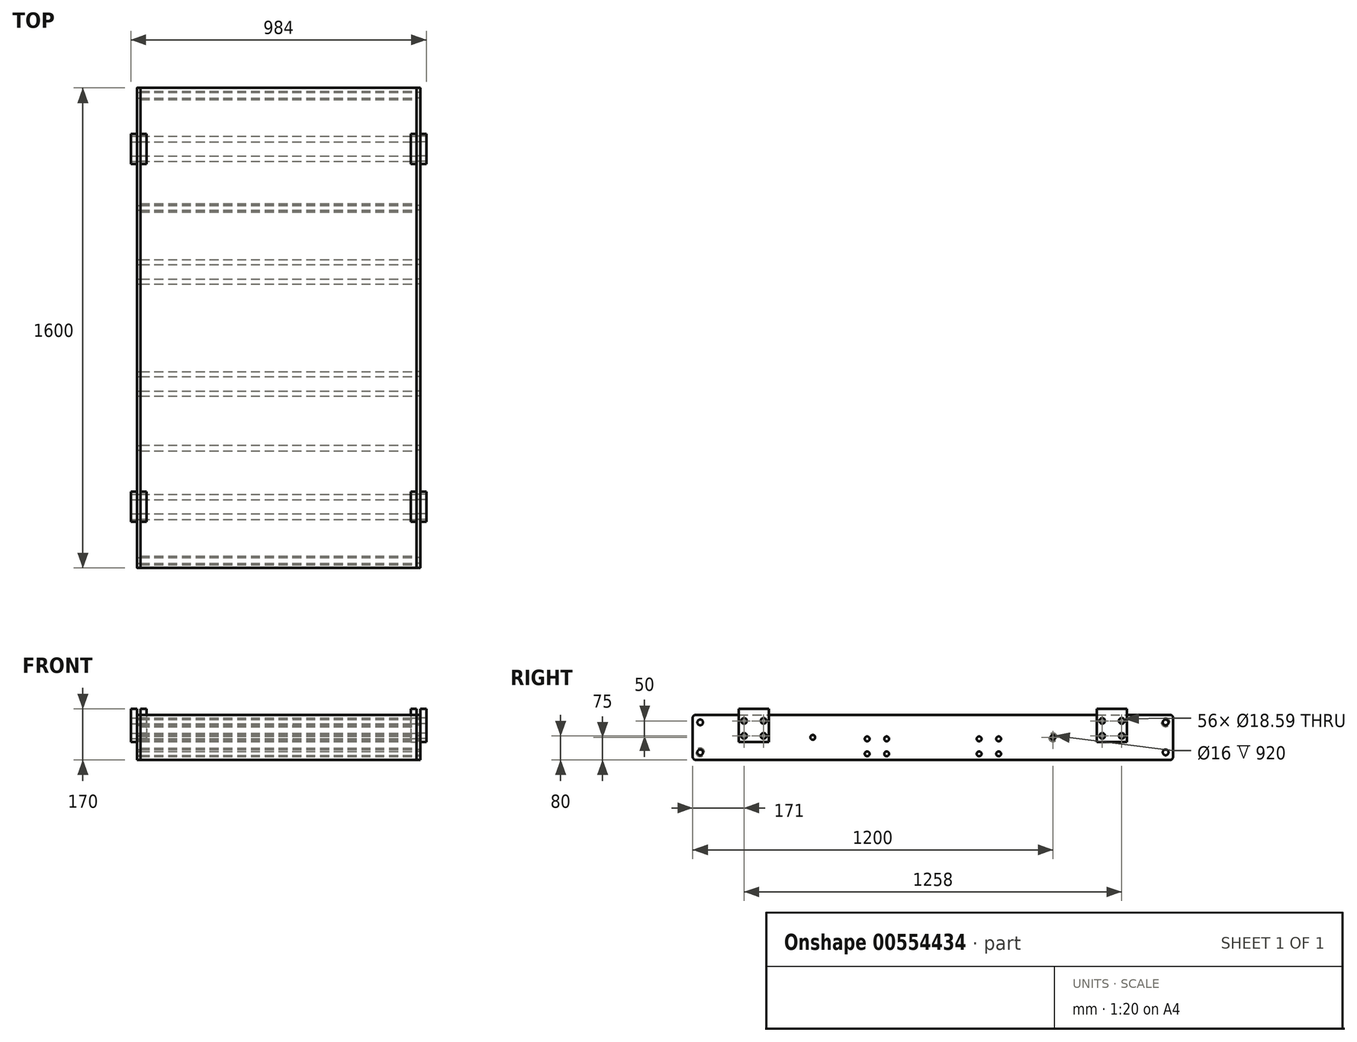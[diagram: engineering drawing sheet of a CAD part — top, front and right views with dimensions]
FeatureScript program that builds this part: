
annotation { "Feature Type Name" : "Feature", "Feature Type Description" : "" }
export const myFeature = defineFeature(function(context is Context, id is Id, definition is map)
    precondition{}
    {
        {
            var Q0;
            Q0=qCreatedBy(makeId("Right.planeOp"),FACE);
            var sketch = newSketch(context, id + "F0", { "sketchPlane" : qUnion([Q0])});
            skLineSegment(sketch, "E0.bottom", {"start": v(-790, 75) * mm, "end": v(790, 75) * mm});
            skLineSegment(sketch, "E0.top", {"start": v(-790, -75) * mm, "end": v(790, -75) * mm});
            skLineSegment(sketch, "E0.left", {"start": v(-800, 65) * mm, "end": v(-800, -65) * mm});
            skLineSegment(sketch, "E0.right", {"start": v(800, 65) * mm, "end": v(800, -65) * mm});
            skPoint(sketch, "E0.middle", {"position": v(0, 0) * mm});
            skLineSegment(sketch, "E1", {"start": v(0, 0) * mm, "end": v(610, 0) * mm, "construction": true});
            skLineSegment(sketch, "E2", {"start": v(0, 0) * mm, "end": v(-610, 0) * mm, "construction": true});
            skLineSegment(sketch, "E3.0", {"start": v(-800, -36.9) * mm, "end": v(800, -36.9) * mm, "construction": true});
            skLineSegment(sketch, "E4.0", {"start": v(-800, 36.9) * mm, "end": v(800, 36.9) * mm, "construction": true});
            skLineSegment(sketch, "E5", {"start": v(610, 36.9) * mm, "end": v(610, -36.9) * mm, "construction": true});
            skLineSegment(sketch, "E6", {"start": v(-610, 36.9) * mm, "end": v(-610, -36.9) * mm, "construction": true});
            skLineSegment(sketch, "E7", {"start": v(610, -36.9) * mm, "end": v(610, -86.9) * mm, "construction": true});
            skPoint(sketch, "E8.visualSharp", {"position": v(-800, 75) * mm});
            skArc(sketch, "E8.filletArc", {"start": v(-790, 75) * mm, "mid": v(-797.07, 72.07) * mm, "end": v(-800, 65) * mm});
            skPoint(sketch, "E9.visualSharp", {"position": v(-800, -75) * mm});
            skArc(sketch, "E9.filletArc", {"start": v(-800, -65) * mm, "mid": v(-797.07, -72.07) * mm, "end": v(-790, -75) * mm});
            skPoint(sketch, "E10.visualSharp", {"position": v(800, 75) * mm});
            skArc(sketch, "E10.filletArc", {"start": v(800, 65) * mm, "mid": v(797.07, 72.07) * mm, "end": v(790, 75) * mm});
            skPoint(sketch, "E11.visualSharp", {"position": v(800, -75) * mm});
            skArc(sketch, "E11.filletArc", {"start": v(790, -75) * mm, "mid": v(797.07, -72.07) * mm, "end": v(800, -65) * mm});
            skCircle(sketch, "E12", {"center": v(-775, 50) * mm, "radius": 9.5 * mm});
            skCircle(sketch, "E13.MirrorC", {"center": v(-775, -50) * mm, "radius": 9.5 * mm});
            skCircle(sketch, "E14.MirrorC", {"center": v(775, -50) * mm, "radius": 9.5 * mm});
            skCircle(sketch, "E15.MirrorC", {"center": v(775, 50) * mm, "radius": 9.5 * mm});
            skCircle(sketch, "E16", {"center": v(-400, 0) * mm, "radius": 8 * mm});
            skCircle(sketch, "E17.MirrorC", {"center": v(400, 0) * mm, "radius": 8 * mm});
            skLineSegment(sketch, "E18", {"start": v(645, -75) * mm, "end": v(645, 137.26) * mm, "construction": true});
            skLineSegment(sketch, "E19", {"start": v(-645, -75) * mm, "end": v(-645, 146.68) * mm, "construction": true});
            skLineSegment(sketch, "E20", {"start": v(-645, 92.82) * mm, "end": v(0, 92.82) * mm, "construction": true});
            skPoint(sketch, "E20.endSnap0", {"position": v(0, 75) * mm});
            skLineSegment(sketch, "E21", {"start": v(0, 92.82) * mm, "end": v(645, 92.82) * mm, "construction": true});
            skLineSegment(sketch, "E22.0", {"start": v(-790, 55) * mm, "end": v(790, 55) * mm, "construction": true});
            skLineSegment(sketch, "E23", {"start": v(-629, 92.82) * mm, "end": v(-629, 0) * mm});
            skPoint(sketch, "E24", {"position": v(-629, 5) * mm});
            skPoint(sketch, "E24.positionSnap0", {"position": v(-629, 46.4) * mm});
            skPoint(sketch, "E25", {"position": v(-629, 55) * mm});
            skLineSegment(sketch, "E26.0", {"start": v(-564, 92.82) * mm, "end": v(-564, 0) * mm});
            skPoint(sketch, "E27", {"position": v(-564, 55) * mm});
            skPoint(sketch, "E28", {"position": v(-564, 5) * mm});
            skCircle(sketch, "E29", {"center": v(-629, 55) * mm, "radius": 9.3 * mm});
            skCircle(sketch, "E30", {"center": v(-564, 55) * mm, "radius": 9.3 * mm});
            skCircle(sketch, "E31", {"center": v(-564, 5) * mm, "radius": 9.3 * mm});
            skCircle(sketch, "E32", {"center": v(-629, 5) * mm, "radius": 9.3 * mm});
            skCircle(sketch, "E33.MirrorC", {"center": v(564, 5) * mm, "radius": 9.3 * mm});
            skCircle(sketch, "E34.MirrorC", {"center": v(629, 5) * mm, "radius": 9.3 * mm});
            skCircle(sketch, "E35.MirrorC", {"center": v(564, 55) * mm, "radius": 9.3 * mm});
            skCircle(sketch, "E36.MirrorC", {"center": v(629, 55) * mm, "radius": 9.3 * mm});
            skLineSegment(sketch, "E37", {"start": v(0, 0) * mm, "end": v(0, 142.93) * mm, "construction": true});
            skLineSegment(sketch, "E38", {"start": v(0, 142.93) * mm, "end": v(-235, 142.93) * mm, "construction": true});
            skLineSegment(sketch, "E39", {"start": v(0, 142.93) * mm, "end": v(235, 142.93) * mm, "construction": true});
            skLineSegment(sketch, "E40", {"start": v(235, 142.93) * mm, "end": v(235, -127.95) * mm, "construction": true});
            skLineSegment(sketch, "E41", {"start": v(-235, 142.93) * mm, "end": v(-235, -127.95) * mm, "construction": true});
            skLineSegment(sketch, "E42.0", {"start": v(-790, -55) * mm, "end": v(790, -55) * mm, "construction": true});
            skLineSegment(sketch, "E43.0", {"start": v(-219, 142.93) * mm, "end": v(-219, -127.95) * mm, "construction": true});
            skLineSegment(sketch, "E44.0", {"start": v(-790, -5) * mm, "end": v(790, -5) * mm, "construction": true});
            skPoint(sketch, "E45", {"position": v(-219, -55) * mm});
            skPoint(sketch, "E46", {"position": v(-219, -5) * mm});
            skLineSegment(sketch, "E47.0", {"start": v(-154, 142.93) * mm, "end": v(-154, -127.95) * mm, "construction": true});
            skPoint(sketch, "E48", {"position": v(-154, -5) * mm});
            skPoint(sketch, "E49", {"position": v(-154, -55) * mm});
            skCircle(sketch, "E50", {"center": v(-219, -5) * mm, "radius": 8 * mm});
            skCircle(sketch, "E51", {"center": v(-154, -5) * mm, "radius": 8 * mm});
            skCircle(sketch, "E52", {"center": v(-154, -55) * mm, "radius": 8 * mm});
            skCircle(sketch, "E53", {"center": v(-219, -55) * mm, "radius": 8 * mm});
            skCircle(sketch, "E54.MirrorC", {"center": v(154, -5) * mm, "radius": 8 * mm});
            skCircle(sketch, "E55.MirrorC", {"center": v(154, -55) * mm, "radius": 8 * mm});
            skCircle(sketch, "E56.MirrorC", {"center": v(219, -55) * mm, "radius": 8 * mm});
            skCircle(sketch, "E57.MirrorC", {"center": v(219, -5) * mm, "radius": 8 * mm});
            skSolve(sketch);
        }
        {
            var Q0;
            Q0=makeQuery(id+"F0.imprint","IMPRINT",FACE,{"disambiguationData":[TD([[makeQuery(id+"F0.imprint","IMPRINT",EDGE,{"derivedFrom":sQuery(id+"F0.wireOp",EDGE,"E0.left")}),1.0]])]});
            extrude(context, id + "F1", {"entities" : qUnion([Q0]), "depth" : 12 * mm, "offsetDistance" : 25 * mm});
        }
        {
            var Q0;
            Q0=makeQuery(id+"F1.opExtrude","CAP_FACE",FACE,{"disambiguationData":[OSD([sQuery(id+"F0.wireOp",EDGE,"E0.bottom"),sQuery(id+"F0.wireOp",EDGE,"E0.top"),sQuery(id+"F0.wireOp",EDGE,"E0.left"),sQuery(id+"F0.wireOp",EDGE,"E0.right"),sQuery(id+"F0.wireOp",EDGE,"sr1cu60X-4lZi-7LVJ-xFVm-K4Fg65r3obhm"),sQuery(id+"F0.wireOp",EDGE,"4rQKllCm-Hdzy-0Bmi-uNUE-3bOPHpEbozwK"),sQuery(id+"F0.wireOp",EDGE,"8aabba5c-8e10-4e2c-b561-5c803436a1782"),sQuery(id+"F0.wireOp",EDGE,"336c5a01-986a-4283-aed1-8bb513b211c40.MirrorCS"),sQuery(id+"F0.wireOp",EDGE,"b70281aa-69d9-49bb-9a57-47f4e425237d0.MirrorCS"),sQuery(id+"F0.wireOp",EDGE,"d646013f-764b-4ce0-857a-2f7dcc32abfd0.MirrorCS"),sQuery(id+"F0.wireOp",EDGE,"b3ca8e81-f062-4b9e-8403-7478d7fd07a70.MirrorCS"),sQuery(id+"F0.wireOp",EDGE,"ee615798-c428-4cc2-82aa-255c5212e68f0.MirrorCS"),sQuery(id+"F0.wireOp",EDGE,"0aa7bf7b-4563-4625-8824-31bc94dce9740.MirrorCS"),sQuery(id+"F0.wireOp",EDGE,"2d8c48ff-f9ce-4c43-bf31-033712d8991f0.MirrorCS"),sQuery(id+"F0.wireOp",EDGE,"9a699b9a-cad8-4cf3-8feb-35564c3ac3a00.MirrorCS"),sQuery(id+"F0.wireOp",EDGE,"1f87250a-3edd-4ec6-831e-a1fcd043075a0.MirrorCS"),sQuery(id+"F0.wireOp",EDGE,"E8.filletArc"),sQuery(id+"F0.wireOp",EDGE,"E9.filletArc"),sQuery(id+"F0.wireOp",EDGE,"E10.filletArc"),sQuery(id+"F0.wireOp",EDGE,"E11.filletArc"),sQuery(id+"F0.wireOp",EDGE,"E12"),sQuery(id+"F0.wireOp",EDGE,"E13.MirrorC"),sQuery(id+"F0.wireOp",EDGE,"E14.MirrorC"),sQuery(id+"F0.wireOp",EDGE,"E15.MirrorC"),sQuery(id+"F0.wireOp",EDGE,"E16"),sQuery(id+"F0.wireOp",EDGE,"E17.MirrorC")])],"isStart":true});
            cPlane(context, id + "F2", {"entities" : qUnion([Q0]), "cplaneType" : CPlaneType.OFFSET, "offset" : 460 * mm, "width" : 150 * mm, "height" : 150 * mm});
        }
        {
            var Q0;
            Q0=makeQuery(id+"F1.opExtrude","SWEPT_BODY",BODY,{"disambiguationData":[OSD([sQuery(id+"F0.wireOp",EDGE,"E0.bottom"),sQuery(id+"F0.wireOp",EDGE,"E0.top"),sQuery(id+"F0.wireOp",EDGE,"E0.left"),sQuery(id+"F0.wireOp",EDGE,"E0.right"),sQuery(id+"F0.wireOp",EDGE,"sr1cu60X-4lZi-7LVJ-xFVm-K4Fg65r3obhm"),sQuery(id+"F0.wireOp",EDGE,"4rQKllCm-Hdzy-0Bmi-uNUE-3bOPHpEbozwK"),sQuery(id+"F0.wireOp",EDGE,"8aabba5c-8e10-4e2c-b561-5c803436a1782"),sQuery(id+"F0.wireOp",EDGE,"336c5a01-986a-4283-aed1-8bb513b211c40.MirrorCS"),sQuery(id+"F0.wireOp",EDGE,"b70281aa-69d9-49bb-9a57-47f4e425237d0.MirrorCS"),sQuery(id+"F0.wireOp",EDGE,"d646013f-764b-4ce0-857a-2f7dcc32abfd0.MirrorCS"),sQuery(id+"F0.wireOp",EDGE,"b3ca8e81-f062-4b9e-8403-7478d7fd07a70.MirrorCS"),sQuery(id+"F0.wireOp",EDGE,"ee615798-c428-4cc2-82aa-255c5212e68f0.MirrorCS"),sQuery(id+"F0.wireOp",EDGE,"0aa7bf7b-4563-4625-8824-31bc94dce9740.MirrorCS"),sQuery(id+"F0.wireOp",EDGE,"2d8c48ff-f9ce-4c43-bf31-033712d8991f0.MirrorCS"),sQuery(id+"F0.wireOp",EDGE,"9a699b9a-cad8-4cf3-8feb-35564c3ac3a00.MirrorCS"),sQuery(id+"F0.wireOp",EDGE,"1f87250a-3edd-4ec6-831e-a1fcd043075a0.MirrorCS"),sQuery(id+"F0.wireOp",EDGE,"E8.filletArc"),sQuery(id+"F0.wireOp",EDGE,"E9.filletArc"),sQuery(id+"F0.wireOp",EDGE,"E10.filletArc"),sQuery(id+"F0.wireOp",EDGE,"E11.filletArc"),sQuery(id+"F0.wireOp",EDGE,"E12"),sQuery(id+"F0.wireOp",EDGE,"E13.MirrorC"),sQuery(id+"F0.wireOp",EDGE,"E14.MirrorC"),sQuery(id+"F0.wireOp",EDGE,"E15.MirrorC"),sQuery(id+"F0.wireOp",EDGE,"E16"),sQuery(id+"F0.wireOp",EDGE,"E17.MirrorC")])]});
            var Q1;
            Q1=qCreatedBy(id+"F2.planeOp",FACE);
            mirror(context, id + "F3", {"entities" : qUnion([Q0]), "mirrorPlane" : qUnion([Q1])});
        }
        {
            var Q0;
            Q0=makeQuery(id+"F1.opExtrude","CAP_FACE",FACE,{"disambiguationData":[OSD([sQuery(id+"F0.wireOp",EDGE,"E0.bottom"),sQuery(id+"F0.wireOp",EDGE,"E0.top"),sQuery(id+"F0.wireOp",EDGE,"E0.left"),sQuery(id+"F0.wireOp",EDGE,"E0.right"),sQuery(id+"F0.wireOp",EDGE,"sr1cu60X-4lZi-7LVJ-xFVm-K4Fg65r3obhm"),sQuery(id+"F0.wireOp",EDGE,"4rQKllCm-Hdzy-0Bmi-uNUE-3bOPHpEbozwK"),sQuery(id+"F0.wireOp",EDGE,"8aabba5c-8e10-4e2c-b561-5c803436a1782"),sQuery(id+"F0.wireOp",EDGE,"336c5a01-986a-4283-aed1-8bb513b211c40.MirrorCS"),sQuery(id+"F0.wireOp",EDGE,"b70281aa-69d9-49bb-9a57-47f4e425237d0.MirrorCS"),sQuery(id+"F0.wireOp",EDGE,"d646013f-764b-4ce0-857a-2f7dcc32abfd0.MirrorCS"),sQuery(id+"F0.wireOp",EDGE,"b3ca8e81-f062-4b9e-8403-7478d7fd07a70.MirrorCS"),sQuery(id+"F0.wireOp",EDGE,"ee615798-c428-4cc2-82aa-255c5212e68f0.MirrorCS"),sQuery(id+"F0.wireOp",EDGE,"0aa7bf7b-4563-4625-8824-31bc94dce9740.MirrorCS"),sQuery(id+"F0.wireOp",EDGE,"2d8c48ff-f9ce-4c43-bf31-033712d8991f0.MirrorCS"),sQuery(id+"F0.wireOp",EDGE,"9a699b9a-cad8-4cf3-8feb-35564c3ac3a00.MirrorCS"),sQuery(id+"F0.wireOp",EDGE,"1f87250a-3edd-4ec6-831e-a1fcd043075a0.MirrorCS"),sQuery(id+"F0.wireOp",EDGE,"E8.filletArc"),sQuery(id+"F0.wireOp",EDGE,"E9.filletArc"),sQuery(id+"F0.wireOp",EDGE,"E10.filletArc"),sQuery(id+"F0.wireOp",EDGE,"E11.filletArc"),sQuery(id+"F0.wireOp",EDGE,"E12"),sQuery(id+"F0.wireOp",EDGE,"E13.MirrorC"),sQuery(id+"F0.wireOp",EDGE,"E14.MirrorC"),sQuery(id+"F0.wireOp",EDGE,"E15.MirrorC"),sQuery(id+"F0.wireOp",EDGE,"E16"),sQuery(id+"F0.wireOp",EDGE,"E17.MirrorC")])],"isStart":true});
            var sketch = newSketch(context, id + "F4", { "sketchPlane" : qUnion([Q0])});
            skCircle(sketch, "E58.0", {"center": v(-775, 50) * mm, "radius": 9.5 * mm});
            skCircle(sketch, "E59.0", {"center": v(-775, -50) * mm, "radius": 9.5 * mm});
            skCircle(sketch, "E60.0", {"center": v(-400, 0) * mm, "radius": 8 * mm});
            skCircle(sketch, "E61.0", {"center": v(400, 0) * mm, "radius": 8 * mm});
            skCircle(sketch, "E62.0", {"center": v(775, -50) * mm, "radius": 9.5 * mm});
            skCircle(sketch, "E63.0", {"center": v(775, 50) * mm, "radius": 9.5 * mm});
            skCircle(sketch, "E64", {"center": v(775, 50) * mm, "radius": 14.29 * mm});
            skCircle(sketch, "E65", {"center": v(775, 50) * mm, "radius": 9.53 * mm});
            skCircle(sketch, "E66", {"center": v(400, 0) * mm, "radius": 9.53 * mm});
            skCircle(sketch, "E67", {"center": v(400, 0) * mm, "radius": 14.29 * mm});
            skCircle(sketch, "E68.MirrorC", {"center": v(775, -50) * mm, "radius": 14.29 * mm});
            skCircle(sketch, "E69.MirrorC", {"center": v(775, -50) * mm, "radius": 9.53 * mm});
            skCircle(sketch, "E70.MirrorC", {"center": v(-775, -50) * mm, "radius": 14.29 * mm});
            skCircle(sketch, "E71.MirrorC", {"center": v(-775, 50) * mm, "radius": 14.29 * mm});
            skCircle(sketch, "E72.MirrorC", {"center": v(-775, 50) * mm, "radius": 9.53 * mm});
            skCircle(sketch, "E73.MirrorC", {"center": v(-775, -50) * mm, "radius": 9.53 * mm});
            skCircle(sketch, "E74.MirrorC", {"center": v(-400, 0) * mm, "radius": 9.53 * mm});
            skCircle(sketch, "E75.MirrorC", {"center": v(-400, 0) * mm, "radius": 14.29 * mm});
            skSolve(sketch);
        }
        {
            var Q0;
            Q0=makeQuery(id+"F4.imprint","IMPRINT",FACE,{"disambiguationData":[TD([[makeQuery(id+"F4.imprint","IMPRINT",EDGE,{"derivedFrom":sQuery(id+"F4.wireOp",EDGE,"E71.MirrorC")}),-1.0]])]});
            var Q1;
            Q1=makeQuery(id+"F4.imprint","IMPRINT",FACE,{"disambiguationData":[TD([[makeQuery(id+"F4.imprint","IMPRINT",EDGE,{"derivedFrom":sQuery(id+"F4.wireOp",EDGE,"E70.MirrorC")}),1.0]])]});
            var Q2;
            Q2=makeQuery(id+"F4.imprint","IMPRINT",FACE,{"disambiguationData":[TD([[makeQuery(id+"F4.imprint","IMPRINT",EDGE,{"derivedFrom":sQuery(id+"F4.wireOp",EDGE,"E74.MirrorC")}),1.0]])]});
            var Q3;
            Q3=makeQuery(id+"F4.imprint","IMPRINT",FACE,{"disambiguationData":[TD([[makeQuery(id+"F4.imprint","IMPRINT",EDGE,{"derivedFrom":sQuery(id+"F4.wireOp",EDGE,"E66")}),-1.0]])]});
            var Q4;
            Q4=makeQuery(id+"F4.imprint","IMPRINT",FACE,{"disambiguationData":[TD([[makeQuery(id+"F4.imprint","IMPRINT",EDGE,{"derivedFrom":sQuery(id+"F4.wireOp",EDGE,"E68.MirrorC")}),-1.0]])]});
            var Q5;
            Q5=makeQuery(id+"F4.imprint","IMPRINT",FACE,{"disambiguationData":[TD([[makeQuery(id+"F4.imprint","IMPRINT",EDGE,{"derivedFrom":sQuery(id+"F4.wireOp",EDGE,"E64")}),1.0]])]});
            var Q6;
            Q6=makeQuery(id+"F3.opPattern","COPY",FACE,{"derivedFrom":makeQuery(id+"F1.opExtrude","CAP_FACE",FACE,{"disambiguationData":[OSD([sQuery(id+"F0.wireOp",EDGE,"E0.bottom"),sQuery(id+"F0.wireOp",EDGE,"E0.top"),sQuery(id+"F0.wireOp",EDGE,"E0.left"),sQuery(id+"F0.wireOp",EDGE,"E0.right"),sQuery(id+"F0.wireOp",EDGE,"sr1cu60X-4lZi-7LVJ-xFVm-K4Fg65r3obhm"),sQuery(id+"F0.wireOp",EDGE,"4rQKllCm-Hdzy-0Bmi-uNUE-3bOPHpEbozwK"),sQuery(id+"F0.wireOp",EDGE,"8aabba5c-8e10-4e2c-b561-5c803436a1782"),sQuery(id+"F0.wireOp",EDGE,"336c5a01-986a-4283-aed1-8bb513b211c40.MirrorCS"),sQuery(id+"F0.wireOp",EDGE,"b70281aa-69d9-49bb-9a57-47f4e425237d0.MirrorCS"),sQuery(id+"F0.wireOp",EDGE,"d646013f-764b-4ce0-857a-2f7dcc32abfd0.MirrorCS"),sQuery(id+"F0.wireOp",EDGE,"b3ca8e81-f062-4b9e-8403-7478d7fd07a70.MirrorCS"),sQuery(id+"F0.wireOp",EDGE,"ee615798-c428-4cc2-82aa-255c5212e68f0.MirrorCS"),sQuery(id+"F0.wireOp",EDGE,"0aa7bf7b-4563-4625-8824-31bc94dce9740.MirrorCS"),sQuery(id+"F0.wireOp",EDGE,"2d8c48ff-f9ce-4c43-bf31-033712d8991f0.MirrorCS"),sQuery(id+"F0.wireOp",EDGE,"9a699b9a-cad8-4cf3-8feb-35564c3ac3a00.MirrorCS"),sQuery(id+"F0.wireOp",EDGE,"1f87250a-3edd-4ec6-831e-a1fcd043075a0.MirrorCS"),sQuery(id+"F0.wireOp",EDGE,"E8.filletArc"),sQuery(id+"F0.wireOp",EDGE,"E9.filletArc"),sQuery(id+"F0.wireOp",EDGE,"E10.filletArc"),sQuery(id+"F0.wireOp",EDGE,"E11.filletArc"),sQuery(id+"F0.wireOp",EDGE,"E12"),sQuery(id+"F0.wireOp",EDGE,"E13.MirrorC"),sQuery(id+"F0.wireOp",EDGE,"E14.MirrorC"),sQuery(id+"F0.wireOp",EDGE,"E15.MirrorC"),sQuery(id+"F0.wireOp",EDGE,"E16"),sQuery(id+"F0.wireOp",EDGE,"E17.MirrorC")])],"isStart":true}),"instanceName":"1"});
            extrude(context, id + "F5", {"entities" : qUnion([Q0, Q1, Q2, Q3, Q4, Q5]), "endBound" : BoundingType.UP_TO_SURFACE, "depth" : 720 * mm, "endBoundEntityFace" : qUnion([Q6]), "offsetDistance" : 25 * mm});
        }
        {
            var Q0;
            Q0=makeQuery(id+"F1.opExtrude","CAP_FACE",FACE,{"disambiguationData":[OSD([sQuery(id+"F0.wireOp",EDGE,"E0.bottom"),sQuery(id+"F0.wireOp",EDGE,"E0.top"),sQuery(id+"F0.wireOp",EDGE,"E0.left"),sQuery(id+"F0.wireOp",EDGE,"E0.right"),sQuery(id+"F0.wireOp",EDGE,"sr1cu60X-4lZi-7LVJ-xFVm-K4Fg65r3obhm"),sQuery(id+"F0.wireOp",EDGE,"4rQKllCm-Hdzy-0Bmi-uNUE-3bOPHpEbozwK"),sQuery(id+"F0.wireOp",EDGE,"8aabba5c-8e10-4e2c-b561-5c803436a1782"),sQuery(id+"F0.wireOp",EDGE,"2d8c48ff-f9ce-4c43-bf31-033712d8991f0.MirrorCS"),sQuery(id+"F0.wireOp",EDGE,"9a699b9a-cad8-4cf3-8feb-35564c3ac3a00.MirrorCS"),sQuery(id+"F0.wireOp",EDGE,"1f87250a-3edd-4ec6-831e-a1fcd043075a0.MirrorCS"),sQuery(id+"F0.wireOp",EDGE,"E8.filletArc"),sQuery(id+"F0.wireOp",EDGE,"E9.filletArc"),sQuery(id+"F0.wireOp",EDGE,"E10.filletArc"),sQuery(id+"F0.wireOp",EDGE,"E11.filletArc"),sQuery(id+"F0.wireOp",EDGE,"E12"),sQuery(id+"F0.wireOp",EDGE,"E13.MirrorC"),sQuery(id+"F0.wireOp",EDGE,"E14.MirrorC"),sQuery(id+"F0.wireOp",EDGE,"E15.MirrorC"),sQuery(id+"F0.wireOp",EDGE,"E16"),sQuery(id+"F0.wireOp",EDGE,"E17.MirrorC"),sQuery(id+"F0.wireOp",EDGE,"E29"),sQuery(id+"F0.wireOp",EDGE,"E30"),sQuery(id+"F0.wireOp",EDGE,"E31"),sQuery(id+"F0.wireOp",EDGE,"E32"),sQuery(id+"F0.wireOp",EDGE,"E33.MirrorC"),sQuery(id+"F0.wireOp",EDGE,"E34.MirrorC"),sQuery(id+"F0.wireOp",EDGE,"E35.MirrorC"),sQuery(id+"F0.wireOp",EDGE,"E36.MirrorC")])],"isStart":true});
            cPlane(context, id + "F6", {"entities" : qUnion([Q0]), "cplaneType" : CPlaneType.OFFSET, "offset" : 6 * mm, "oppositeDirection" : true, "width" : 150 * mm, "height" : 150 * mm});
        }
        {
            var Q0;
            Q0=makeQuery(id+"F1.opExtrude","CAP_FACE",FACE,{"disambiguationData":[OSD([sQuery(id+"F0.wireOp",EDGE,"E0.bottom"),sQuery(id+"F0.wireOp",EDGE,"E0.top"),sQuery(id+"F0.wireOp",EDGE,"E0.left"),sQuery(id+"F0.wireOp",EDGE,"E0.right"),sQuery(id+"F0.wireOp",EDGE,"sr1cu60X-4lZi-7LVJ-xFVm-K4Fg65r3obhm"),sQuery(id+"F0.wireOp",EDGE,"4rQKllCm-Hdzy-0Bmi-uNUE-3bOPHpEbozwK"),sQuery(id+"F0.wireOp",EDGE,"8aabba5c-8e10-4e2c-b561-5c803436a1782"),sQuery(id+"F0.wireOp",EDGE,"2d8c48ff-f9ce-4c43-bf31-033712d8991f0.MirrorCS"),sQuery(id+"F0.wireOp",EDGE,"9a699b9a-cad8-4cf3-8feb-35564c3ac3a00.MirrorCS"),sQuery(id+"F0.wireOp",EDGE,"1f87250a-3edd-4ec6-831e-a1fcd043075a0.MirrorCS"),sQuery(id+"F0.wireOp",EDGE,"E8.filletArc"),sQuery(id+"F0.wireOp",EDGE,"E9.filletArc"),sQuery(id+"F0.wireOp",EDGE,"E10.filletArc"),sQuery(id+"F0.wireOp",EDGE,"E11.filletArc"),sQuery(id+"F0.wireOp",EDGE,"E12"),sQuery(id+"F0.wireOp",EDGE,"E13.MirrorC"),sQuery(id+"F0.wireOp",EDGE,"E14.MirrorC"),sQuery(id+"F0.wireOp",EDGE,"E15.MirrorC"),sQuery(id+"F0.wireOp",EDGE,"E16"),sQuery(id+"F0.wireOp",EDGE,"E17.MirrorC"),sQuery(id+"F0.wireOp",EDGE,"E29"),sQuery(id+"F0.wireOp",EDGE,"E30"),sQuery(id+"F0.wireOp",EDGE,"E31"),sQuery(id+"F0.wireOp",EDGE,"E32"),sQuery(id+"F0.wireOp",EDGE,"E33.MirrorC"),sQuery(id+"F0.wireOp",EDGE,"E34.MirrorC"),sQuery(id+"F0.wireOp",EDGE,"E35.MirrorC"),sQuery(id+"F0.wireOp",EDGE,"E36.MirrorC")])],"isStart":false});
            var sketch = newSketch(context, id + "F7", { "sketchPlane" : qUnion([Q0])});
            skCircle(sketch, "E76.0", {"center": v(-564, 5) * mm, "radius": 9.3 * mm});
            skCircle(sketch, "E77.0", {"center": v(-564, 55) * mm, "radius": 9.3 * mm});
            skCircle(sketch, "E78.0", {"center": v(-629, 55) * mm, "radius": 9.3 * mm});
            skCircle(sketch, "E79.0", {"center": v(-629, 5) * mm, "radius": 9.3 * mm});
            skLineSegment(sketch, "E80", {"start": v(-564, 55) * mm, "end": v(-546.5, 55) * mm, "construction": true});
            skLineSegment(sketch, "E81", {"start": v(-564, 5) * mm, "end": v(-546.5, 5) * mm, "construction": true});
            skLineSegment(sketch, "E82", {"start": v(-629, 55) * mm, "end": v(-646.5, 55) * mm, "construction": true});
            skLineSegment(sketch, "E83", {"start": v(-629, 5) * mm, "end": v(-646.5, 5) * mm, "construction": true});
            skLineSegment(sketch, "E84", {"start": v(-629, 5) * mm, "end": v(-564, 5) * mm, "construction": true});
            skLineSegment(sketch, "E85", {"start": v(-596.5, 5) * mm, "end": v(-596.5, -15) * mm, "construction": true});
            skLineSegment(sketch, "E86", {"start": v(-646.5, -15) * mm, "end": v(-546.5, -15) * mm});
            skLineSegment(sketch, "E87", {"start": v(-596.5, 5) * mm, "end": v(-596.5, 95) * mm, "construction": true});
            skLineSegment(sketch, "E88", {"start": v(-546.5, -15) * mm, "end": v(-546.5, 95) * mm});
            skLineSegment(sketch, "E89", {"start": v(-546.5, 95) * mm, "end": v(-646.5, 95) * mm});
            skLineSegment(sketch, "E90", {"start": v(-646.5, 95) * mm, "end": v(-646.5, -15) * mm});
            skLineSegment(sketch, "E91.MirrorCS", {"start": v(546.5, -15) * mm, "end": v(546.5, 95) * mm});
            skLineSegment(sketch, "E92.MirrorCS", {"start": v(546.5, 95) * mm, "end": v(646.5, 95) * mm});
            skLineSegment(sketch, "E93.MirrorCS", {"start": v(646.5, 95) * mm, "end": v(646.5, -15) * mm});
            skLineSegment(sketch, "E94.MirrorCS", {"start": v(646.5, -15) * mm, "end": v(546.5, -15) * mm});
            skCircle(sketch, "E95.MirrorC", {"center": v(564, 5) * mm, "radius": 9.3 * mm});
            skCircle(sketch, "E96.MirrorC", {"center": v(564, 55) * mm, "radius": 9.3 * mm});
            skCircle(sketch, "E97.MirrorC", {"center": v(629, 55) * mm, "radius": 9.3 * mm});
            skCircle(sketch, "E98.MirrorC", {"center": v(629, 5) * mm, "radius": 9.3 * mm});
            skSolve(sketch);
        }
        {
            var Q0;
            Q0=makeQuery(id+"F7.imprint","IMPRINT",FACE,{"disambiguationData":[TD([[makeQuery(id+"F7.imprint","IMPRINT",EDGE,{"derivedFrom":sQuery(id+"F7.wireOp",EDGE,"E76.0")}),-1.0]])]});
            var Q1;
            {var subQ0=sQuery(id+"F7.wireOp",EDGE,"E89");Q1=makeQuery(id+"F7.imprint","IMPRINT",FACE,{"disambiguationData":[TD([[makeQuery(id+"F7.imprint","IMPRINT",EDGE,{"derivedFrom":subQ0}),1.0]])]});}
            var Q2;
            {var subQ0=sQuery(id+"F7.wireOp",EDGE,"E92.MirrorCS");Q2=makeQuery(id+"F7.imprint","IMPRINT",FACE,{"disambiguationData":[TD([[makeQuery(id+"F7.imprint","IMPRINT",EDGE,{"derivedFrom":subQ0}),-1.0]])]});}
            var Q3;
            {var subQ0=sQuery(id+"F7.wireOp",EDGE,"E94.MirrorCS");Q3=makeQuery(id+"F7.imprint","IMPRINT",FACE,{"disambiguationData":[TD([[makeQuery(id+"F7.imprint","IMPRINT",EDGE,{"derivedFrom":subQ0}),-1.0]])]});}
            extrude(context, id + "F8", {"entities" : qUnion([Q0, Q1, Q2, Q3]), "depth" : 20 * mm, "offsetDistance" : 25 * mm});
        }
        {
            var Q0;
            Q0=makeQuery(id+"F8.opExtrude","SWEPT_BODY",BODY,{"disambiguationData":[OSD([sQuery(id+"F7.wireOp",EDGE,"E76.0"),sQuery(id+"F7.wireOp",EDGE,"E77.0"),sQuery(id+"F7.wireOp",EDGE,"E78.0"),sQuery(id+"F7.wireOp",EDGE,"E79.0"),sQuery(id+"F7.wireOp",EDGE,"E86"),sQuery(id+"F7.wireOp",EDGE,"E88"),sQuery(id+"F7.wireOp",EDGE,"E89"),sQuery(id+"F7.wireOp",EDGE,"E90")])]});
            var Q1;
            Q1=makeQuery(id+"F8.opExtrude","SWEPT_BODY",BODY,{"disambiguationData":[OSD([sQuery(id+"F7.wireOp",EDGE,"E91.MirrorCS"),sQuery(id+"F7.wireOp",EDGE,"E92.MirrorCS"),sQuery(id+"F7.wireOp",EDGE,"E93.MirrorCS"),sQuery(id+"F7.wireOp",EDGE,"E94.MirrorCS"),sQuery(id+"F7.wireOp",EDGE,"E95.MirrorC"),sQuery(id+"F7.wireOp",EDGE,"E96.MirrorC"),sQuery(id+"F7.wireOp",EDGE,"E97.MirrorC"),sQuery(id+"F7.wireOp",EDGE,"E98.MirrorC")])]});
            var Q2;
            Q2=qCreatedBy(id+"F6.planeOp",FACE);
            mirror(context, id + "F9", {"entities" : qUnion([Q0, Q1]), "mirrorPlane" : qUnion([Q2])});
        }
        {
            var Q0;
            Q0=makeQuery(id+"F8.opExtrude","SWEPT_BODY",BODY,{"disambiguationData":[OSD([sQuery(id+"F7.wireOp",EDGE,"E76.0"),sQuery(id+"F7.wireOp",EDGE,"E77.0"),sQuery(id+"F7.wireOp",EDGE,"E78.0"),sQuery(id+"F7.wireOp",EDGE,"E79.0"),sQuery(id+"F7.wireOp",EDGE,"E86"),sQuery(id+"F7.wireOp",EDGE,"E88"),sQuery(id+"F7.wireOp",EDGE,"E89"),sQuery(id+"F7.wireOp",EDGE,"E90")])]});
            var Q1;
            Q1=makeQuery(id+"F9.opPattern","COPY",BODY,{"derivedFrom":makeQuery(id+"F8.opExtrude","SWEPT_BODY",BODY,{"disambiguationData":[OSD([sQuery(id+"F7.wireOp",EDGE,"E76.0"),sQuery(id+"F7.wireOp",EDGE,"E77.0"),sQuery(id+"F7.wireOp",EDGE,"E78.0"),sQuery(id+"F7.wireOp",EDGE,"E79.0"),sQuery(id+"F7.wireOp",EDGE,"E86"),sQuery(id+"F7.wireOp",EDGE,"E88"),sQuery(id+"F7.wireOp",EDGE,"E89"),sQuery(id+"F7.wireOp",EDGE,"E90")])]}),"instanceName":"1"});
            var Q2;
            Q2=makeQuery(id+"F9.opPattern","COPY",BODY,{"derivedFrom":makeQuery(id+"F8.opExtrude","SWEPT_BODY",BODY,{"disambiguationData":[OSD([sQuery(id+"F7.wireOp",EDGE,"E91.MirrorCS"),sQuery(id+"F7.wireOp",EDGE,"E92.MirrorCS"),sQuery(id+"F7.wireOp",EDGE,"E93.MirrorCS"),sQuery(id+"F7.wireOp",EDGE,"E94.MirrorCS"),sQuery(id+"F7.wireOp",EDGE,"E95.MirrorC"),sQuery(id+"F7.wireOp",EDGE,"E96.MirrorC"),sQuery(id+"F7.wireOp",EDGE,"E97.MirrorC"),sQuery(id+"F7.wireOp",EDGE,"E98.MirrorC")])]}),"instanceName":"1"});
            var Q3;
            Q3=makeQuery(id+"F8.opExtrude","SWEPT_BODY",BODY,{"disambiguationData":[OSD([sQuery(id+"F7.wireOp",EDGE,"E91.MirrorCS"),sQuery(id+"F7.wireOp",EDGE,"E92.MirrorCS"),sQuery(id+"F7.wireOp",EDGE,"E93.MirrorCS"),sQuery(id+"F7.wireOp",EDGE,"E94.MirrorCS"),sQuery(id+"F7.wireOp",EDGE,"E95.MirrorC"),sQuery(id+"F7.wireOp",EDGE,"E96.MirrorC"),sQuery(id+"F7.wireOp",EDGE,"E97.MirrorC"),sQuery(id+"F7.wireOp",EDGE,"E98.MirrorC")])]});
            var Q4;
            Q4=qCreatedBy(id+"F2.planeOp",FACE);
            mirror(context, id + "F10", {"entities" : qUnion([Q0, Q1, Q2, Q3]), "mirrorPlane" : qUnion([Q4])});
        }
    });
